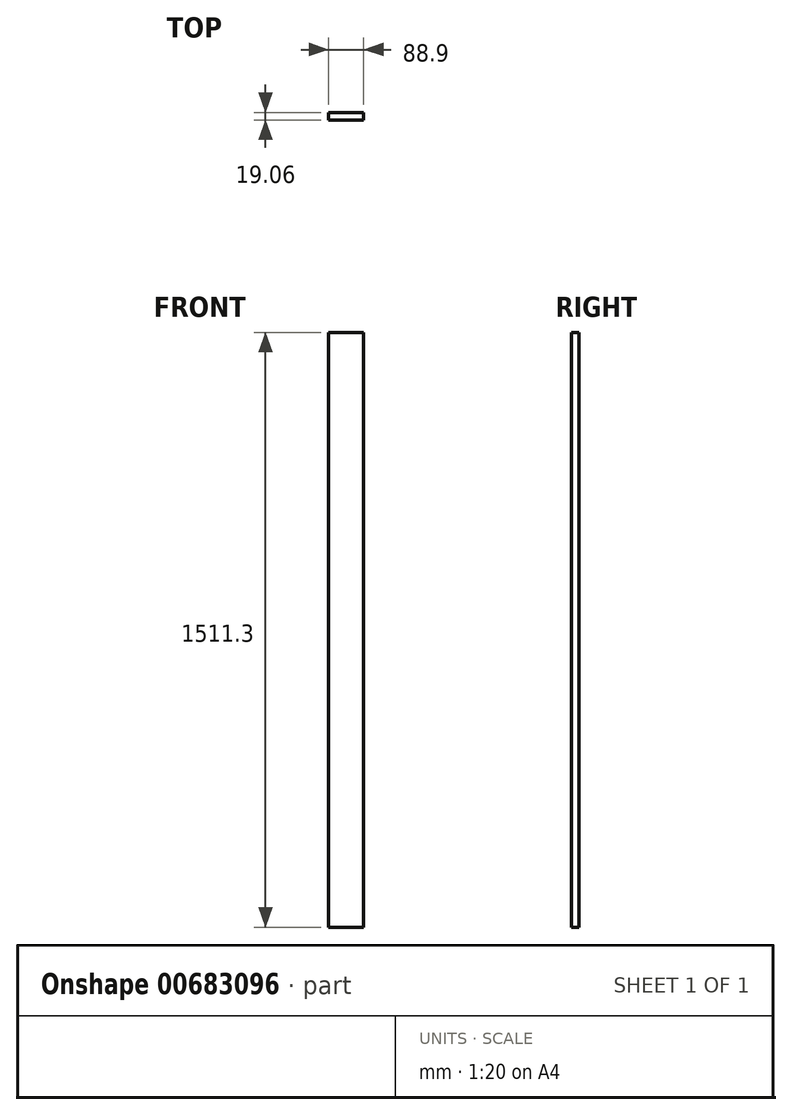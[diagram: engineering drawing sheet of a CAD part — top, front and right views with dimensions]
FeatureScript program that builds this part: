
annotation { "Feature Type Name" : "Feature", "Feature Type Description" : "" }
export const myFeature = defineFeature(function(context is Context, id is Id, definition is map)
    precondition{}
    {
        {
            var Q0;
            Q0=qCreatedBy(makeId("Top.planeOp"),FACE);
            var sketch = newSketch(context, id + "F0", { "sketchPlane" : qUnion([Q0])});
            skLineSegment(sketch, "E0.bottom", {"start": v(44.45, 9.53) * mm, "end": v(-44.45, 9.53) * mm});
            skLineSegment(sketch, "E0.top", {"start": v(44.45, -9.52) * mm, "end": v(-44.45, -9.52) * mm});
            skLineSegment(sketch, "E0.left", {"start": v(44.45, 9.52) * mm, "end": v(44.45, -9.52) * mm});
            skLineSegment(sketch, "E0.right", {"start": v(-44.45, 9.52) * mm, "end": v(-44.45, -9.52) * mm});
            skPoint(sketch, "E0.middle", {"position": v(0, 0) * mm});
            skSolve(sketch);
        }
        {
            var Q0;
            Q0=qSketchRegion(id+"F0",true);
            extrude(context, id + "F1", {"entities" : qUnion([Q0]), "depth" : 1511.3 * mm, "offsetDistance" : 25.4 * mm});
        }
    });
